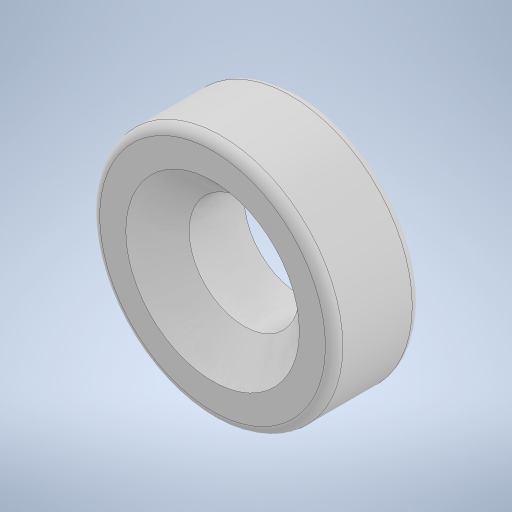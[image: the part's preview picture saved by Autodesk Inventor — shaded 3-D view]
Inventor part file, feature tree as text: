
AUTODESK INVENTOR PART (.ipt)
format: ipt  version: 2023 (Build 270158000, 158)  size: 257,536 bytes
history: native  units: mm
features: sketch x1, extrude x1, hole x1, fillet x1
ambient origin geometry x8: Origin, YZ Plane, XZ Plane, XY Plane, X Axis, Y Axis, Z Axis, Center Point
bodies: Solid1 (feature_tree)
feature tree (4):
  sketch  "Sketch1"  dims[d0=14.0mm d2=5.0mm d3=0.0mm d4=6.35mm d5=6.0mm d6=10.0mm d7=2.0mm d8=90.0deg d9=8.0mm d10=20.594885mm d11=0.5mm]
  extrude  "Extrusion1"  Depth=5.0mm TaperAngle=0.0deg
  hole  "Hole1"  [1 undecoded]
  fillet  "Fillet1"  [1 undecoded]
note: 2 required parameter values undecoded (feature->parameter linkage not recoverable at this tier; creation-order binding heuristic only, values carry confidence <= 0.55)
